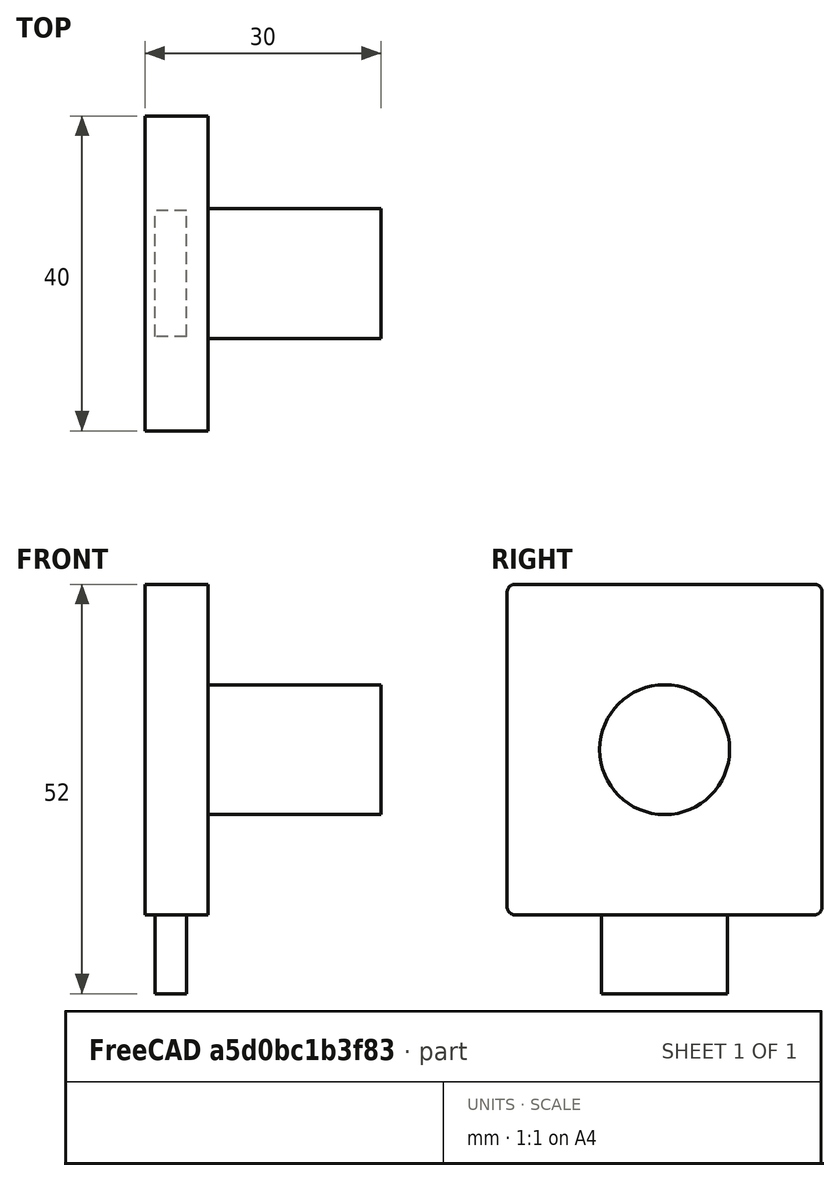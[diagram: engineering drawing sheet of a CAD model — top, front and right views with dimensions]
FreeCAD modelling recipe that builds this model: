
FCSTD DOCUMENT  (FreeCAD 0.15R4671 (Git))
Label: cabinet_lock_40x42mm
License: All rights reserved
LicenseURL: http://es.wikipedia.org/wiki/Todos_los_derechos_reservados
objects: Part::Box×3, Part::MultiFuse×3, Part::Cut×2, Part::Cylinder×1, Part::Fillet×1
note: 10 computed .brp shape members not serialized (recipe doc carries the construction recipe); baked Part::Feature solids carry a one-line shape summary decoded from their .brp

FEATURE [Part::Box] Box  label="Base Cerradura"
  Height = 42
  Length = 8
  Placement = pos=(474,40,792) rot=(0,0,1;0rad)
  Width = 40
FEATURE [Part::Cylinder] Cylinder  label="Cerradura"
  Angle = 360
  Height = 22
  Placement = pos=(482,60,813) rot=(0,1,0;1.5708rad)
  Radius = 8.25
FEATURE [Part::MultiFuse] Fusion  label="Cerradura y Base"
  Shapes = -> [Box,Cylinder]
FEATURE [Part::Box] Box001  label="Lengüeta Cierre"
  Height = 12
  Length = 4
  Placement = pos=(475.25,52,782) rot=(0,0,1;0rad)
  Width = 16
FEATURE [Part::MultiFuse] Fusion001  label="Cierre Completo"
  Shapes = -> [Fusion,Box001]
FEATURE [Part::Box] Box002  label="Hueco Llave"
  Height = 10
  Length = 4
  Placement = pos=(502,58.5,808) rot=(0,0,1;0rad)
  Width = 3
FEATURE [Part::Cut] Cut  label="Cierre Completo con Hueco Llave"
  Base = -> Fusion001
  Tool = -> Box002
FEATURE [Part::Cut] Cut001
  Base = -> Fusion
  Tool = -> Box002
FEATURE [Part::MultiFuse] Fusion002  label="Cierre"
  Shapes = -> [Cut,Box001,Fusion001,Cut001]
FEATURE [Part::Fillet] Fillet
  Base = -> Fusion002
  Edges = 4 edges r=1: [Edge14,Edge15,Edge21,Edge23]
